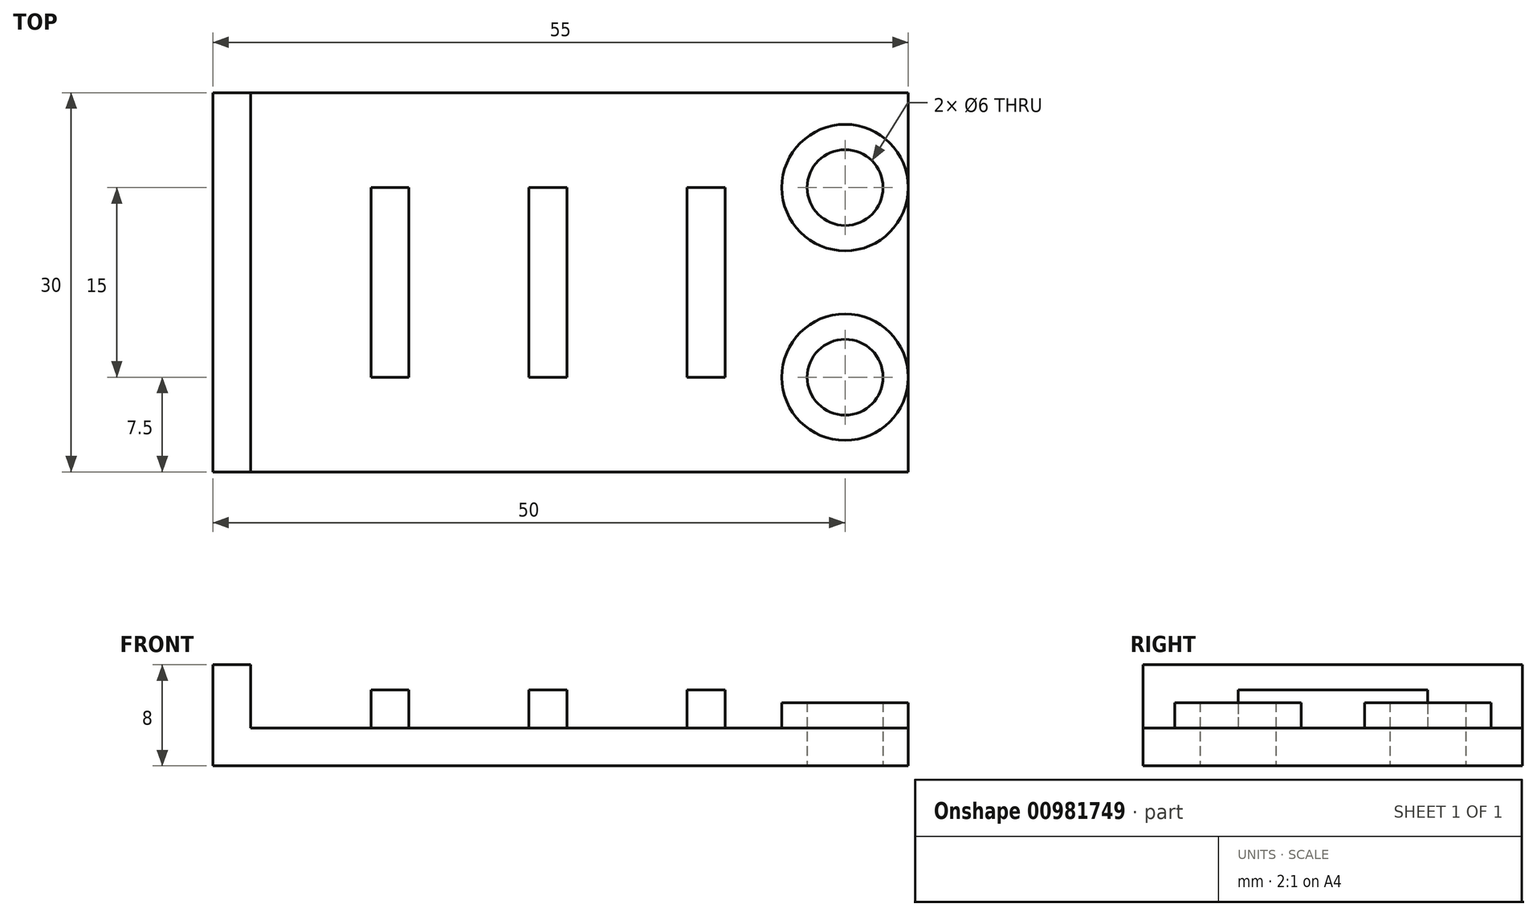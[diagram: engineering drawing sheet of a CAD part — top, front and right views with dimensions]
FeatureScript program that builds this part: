
annotation { "Feature Type Name" : "Feature", "Feature Type Description" : "" }
export const myFeature = defineFeature(function(context is Context, id is Id, definition is map)
    precondition{}
    {
        {
            var Q0;
            Q0=qCreatedBy(makeId("Top.planeOp"),FACE);
            var sketch = newSketch(context, id + "F0", { "sketchPlane" : qUnion([Q0])});
            skLineSegment(sketch, "E0.bottom", {"start": v(0, 30) * mm, "end": v(52, 30) * mm});
            skLineSegment(sketch, "E0.top", {"start": v(0, 0) * mm, "end": v(52, 0) * mm});
            skLineSegment(sketch, "E0.left", {"start": v(0, 30) * mm, "end": v(0, 0) * mm});
            skLineSegment(sketch, "E0.right", {"start": v(52, 30) * mm, "end": v(52, 0) * mm});
            skCircle(sketch, "E1", {"center": v(47, 22.5) * mm, "radius": 3 * mm});
            skCircle(sketch, "E2", {"center": v(47, 7.5) * mm, "radius": 3 * mm});
            skLineSegment(sketch, "E3", {"start": v(47, 22.5) * mm, "end": v(47, 7.5) * mm, "construction": true});
            skLineSegment(sketch, "E4", {"start": v(47, 15) * mm, "end": v(52, 15) * mm, "construction": true});
            skLineSegment(sketch, "E5.bottom", {"start": v(9.5, 22.5) * mm, "end": v(12.5, 22.5) * mm});
            skLineSegment(sketch, "E5.top", {"start": v(9.5, 7.5) * mm, "end": v(12.5, 7.5) * mm});
            skLineSegment(sketch, "E5.left", {"start": v(9.5, 22.5) * mm, "end": v(9.5, 7.5) * mm});
            skLineSegment(sketch, "E5.right", {"start": v(12.5, 22.5) * mm, "end": v(12.5, 7.5) * mm});
            skLineSegment(sketch, "E6.bottom", {"start": v(22, 22.5) * mm, "end": v(25, 22.5) * mm});
            skLineSegment(sketch, "E6.top", {"start": v(22, 7.5) * mm, "end": v(25, 7.5) * mm});
            skLineSegment(sketch, "E6.left", {"start": v(22, 22.5) * mm, "end": v(22, 7.5) * mm});
            skLineSegment(sketch, "E6.right", {"start": v(25, 22.5) * mm, "end": v(25, 7.5) * mm});
            skLineSegment(sketch, "E7.bottom", {"start": v(34.5, 22.5) * mm, "end": v(37.5, 22.5) * mm});
            skLineSegment(sketch, "E7.top", {"start": v(34.5, 7.5) * mm, "end": v(37.5, 7.5) * mm});
            skLineSegment(sketch, "E7.left", {"start": v(34.5, 22.5) * mm, "end": v(34.5, 7.5) * mm});
            skLineSegment(sketch, "E7.right", {"start": v(37.5, 22.5) * mm, "end": v(37.5, 7.5) * mm});
            skLineSegment(sketch, "E8", {"start": v(9.5, 22.5) * mm, "end": v(0, 22.5) * mm, "construction": true});
            skLineSegment(sketch, "E9", {"start": v(22, 22.5) * mm, "end": v(12.5, 22.5) * mm, "construction": true});
            skLineSegment(sketch, "E10", {"start": v(34.5, 22.5) * mm, "end": v(25, 22.5) * mm, "construction": true});
            skLineSegment(sketch, "E11", {"start": v(37.5, 22.5) * mm, "end": v(47, 22.5) * mm, "construction": true});
            skLineSegment(sketch, "E12", {"start": v(0, 30) * mm, "end": v(-3, 30) * mm});
            skLineSegment(sketch, "E13", {"start": v(-3, 30) * mm, "end": v(-3, 0) * mm});
            skLineSegment(sketch, "E14", {"start": v(-3, 0) * mm, "end": v(0, 0) * mm});
            skCircle(sketch, "E15", {"center": v(47, 22.5) * mm, "radius": 5 * mm});
            skCircle(sketch, "E16", {"center": v(47, 7.5) * mm, "radius": 5 * mm});
            skSolve(sketch);
        }
        {
            var Q0;
            Q0=makeQuery(id+"F0.imprint","IMPRINT",FACE,{"disambiguationData":[TD([[makeQuery(id+"F0.imprint","IMPRINT",EDGE,{"derivedFrom":sQuery(id+"F0.wireOp",EDGE,"E0.bottom")}),-1.0]])]});
            var Q1;
            Q1=makeQuery(id+"F0.imprint","IMPRINT",FACE,{"disambiguationData":[TD([[makeQuery(id+"F0.imprint","IMPRINT",EDGE,{"derivedFrom":sQuery(id+"F0.wireOp",EDGE,"E2")}),-1.0]])]});
            var Q2;
            Q2=makeQuery(id+"F0.imprint","IMPRINT",FACE,{"disambiguationData":[TD([[makeQuery(id+"F0.imprint","IMPRINT",EDGE,{"derivedFrom":sQuery(id+"F0.wireOp",EDGE,"E1")}),-1.0]])]});
            extrude(context, id + "F1", {"entities" : qUnion([Q0, Q1, Q2]), "offsetDistance" : 25 * mm, "depth" : 3 * mm});
        }
        {
            var Q0;
            Q0=makeQuery(id+"F0.imprint","IMPRINT",FACE,{"disambiguationData":[TD([[makeQuery(id+"F0.imprint","IMPRINT",EDGE,{"derivedFrom":sQuery(id+"F0.wireOp",EDGE,"E0.left")}),-1.0]])]});
            var Q1;
            Q1=makeQuery(id+"F1.opExtrude","CAP_FACE",FACE,{"disambiguationData":[OSD([sQuery(id+"F0.wireOp",EDGE,"E0.bottom"),sQuery(id+"F0.wireOp",EDGE,"E0.top"),sQuery(id+"F0.wireOp",EDGE,"E0.left"),sQuery(id+"F0.wireOp",EDGE,"E0.right"),sQuery(id+"F0.wireOp",EDGE,"E1"),sQuery(id+"F0.wireOp",EDGE,"E2"),sQuery(id+"F0.wireOp",EDGE,"E5.bottom"),sQuery(id+"F0.wireOp",EDGE,"E5.top"),sQuery(id+"F0.wireOp",EDGE,"E5.left"),sQuery(id+"F0.wireOp",EDGE,"E5.right"),sQuery(id+"F0.wireOp",EDGE,"E6.bottom"),sQuery(id+"F0.wireOp",EDGE,"E6.top"),sQuery(id+"F0.wireOp",EDGE,"E6.left"),sQuery(id+"F0.wireOp",EDGE,"E6.right"),sQuery(id+"F0.wireOp",EDGE,"E7.bottom"),sQuery(id+"F0.wireOp",EDGE,"E7.top"),sQuery(id+"F0.wireOp",EDGE,"E7.left"),sQuery(id+"F0.wireOp",EDGE,"E7.right")])],"isStart":false});
            extrude(context, id + "F2", {"entities" : qUnion([Q0]), "operationType" : NewBodyOperationType.ADD, "endBound" : BoundingType.UP_TO_SURFACE, "endBoundEntityFace" : qUnion([Q1]), "hasOffset" : true, "offsetDistance" : 5 * mm, "offsetOppositeDirection" : true, "depth" : 8 * mm});
        }
        {
            var Q0;
            Q0=makeQuery(id+"F0.imprint","IMPRINT",FACE,{"disambiguationData":[TD([[makeQuery(id+"F0.imprint","IMPRINT",EDGE,{"derivedFrom":sQuery(id+"F0.wireOp",EDGE,"E5.bottom")}),-1.0]])]});
            var Q1;
            Q1=makeQuery(id+"F0.imprint","IMPRINT",FACE,{"disambiguationData":[TD([[makeQuery(id+"F0.imprint","IMPRINT",EDGE,{"derivedFrom":sQuery(id+"F0.wireOp",EDGE,"E6.bottom")}),-1.0]])]});
            var Q2;
            Q2=makeQuery(id+"F0.imprint","IMPRINT",FACE,{"disambiguationData":[TD([[makeQuery(id+"F0.imprint","IMPRINT",EDGE,{"derivedFrom":sQuery(id+"F0.wireOp",EDGE,"E7.bottom")}),-1.0]])]});
            var Q3;
            Q3=makeQuery(id+"F1.opExtrude","CAP_FACE",FACE,{"disambiguationData":[OSD([sQuery(id+"F0.wireOp",EDGE,"E0.bottom"),sQuery(id+"F0.wireOp",EDGE,"E0.top"),sQuery(id+"F0.wireOp",EDGE,"E0.left"),sQuery(id+"F0.wireOp",EDGE,"E0.right"),sQuery(id+"F0.wireOp",EDGE,"E1"),sQuery(id+"F0.wireOp",EDGE,"E2"),sQuery(id+"F0.wireOp",EDGE,"E5.bottom"),sQuery(id+"F0.wireOp",EDGE,"E5.top"),sQuery(id+"F0.wireOp",EDGE,"E5.left"),sQuery(id+"F0.wireOp",EDGE,"E5.right"),sQuery(id+"F0.wireOp",EDGE,"E6.bottom"),sQuery(id+"F0.wireOp",EDGE,"E6.top"),sQuery(id+"F0.wireOp",EDGE,"E6.left"),sQuery(id+"F0.wireOp",EDGE,"E6.right"),sQuery(id+"F0.wireOp",EDGE,"E7.bottom"),sQuery(id+"F0.wireOp",EDGE,"E7.top"),sQuery(id+"F0.wireOp",EDGE,"E7.left"),sQuery(id+"F0.wireOp",EDGE,"E7.right")])],"isStart":false});
            extrude(context, id + "F3", {"entities" : qUnion([Q0, Q1, Q2]), "operationType" : NewBodyOperationType.ADD, "endBound" : BoundingType.UP_TO_SURFACE, "endBoundEntityFace" : qUnion([Q3]), "hasOffset" : true, "offsetDistance" : 3 * mm, "offsetOppositeDirection" : true, "depth" : 6 * mm});
        }
        {
            var Q0;
            Q0=makeQuery(id+"F0.imprint","IMPRINT",FACE,{"disambiguationData":[TD([[makeQuery(id+"F0.imprint","IMPRINT",EDGE,{"derivedFrom":sQuery(id+"F0.wireOp",EDGE,"E1")}),-1.0]])]});
            var Q1;
            Q1=makeQuery(id+"F0.imprint","IMPRINT",FACE,{"disambiguationData":[TD([[makeQuery(id+"F0.imprint","IMPRINT",EDGE,{"derivedFrom":sQuery(id+"F0.wireOp",EDGE,"E2")}),-1.0]])]});
            var Q2;
            Q2=makeQuery(id+"F1.opExtrude","CAP_FACE",FACE,{"disambiguationData":[OSD([sQuery(id+"F0.wireOp",EDGE,"E0.bottom"),sQuery(id+"F0.wireOp",EDGE,"E0.top"),sQuery(id+"F0.wireOp",EDGE,"E0.left"),sQuery(id+"F0.wireOp",EDGE,"E0.right"),sQuery(id+"F0.wireOp",EDGE,"E1"),sQuery(id+"F0.wireOp",EDGE,"E2"),sQuery(id+"F0.wireOp",EDGE,"E5.bottom"),sQuery(id+"F0.wireOp",EDGE,"E5.top"),sQuery(id+"F0.wireOp",EDGE,"E5.left"),sQuery(id+"F0.wireOp",EDGE,"E5.right"),sQuery(id+"F0.wireOp",EDGE,"E6.bottom"),sQuery(id+"F0.wireOp",EDGE,"E6.top"),sQuery(id+"F0.wireOp",EDGE,"E6.left"),sQuery(id+"F0.wireOp",EDGE,"E6.right"),sQuery(id+"F0.wireOp",EDGE,"E7.bottom"),sQuery(id+"F0.wireOp",EDGE,"E7.top"),sQuery(id+"F0.wireOp",EDGE,"E7.left"),sQuery(id+"F0.wireOp",EDGE,"E7.right")])],"isStart":false});
            extrude(context, id + "F4", {"entities" : qUnion([Q0, Q1]), "operationType" : NewBodyOperationType.ADD, "endBound" : BoundingType.UP_TO_SURFACE, "endBoundEntityFace" : qUnion([Q2]), "hasOffset" : true, "offsetDistance" : 2 * mm, "offsetOppositeDirection" : true, "depth" : 1 * mm});
        }
    });
